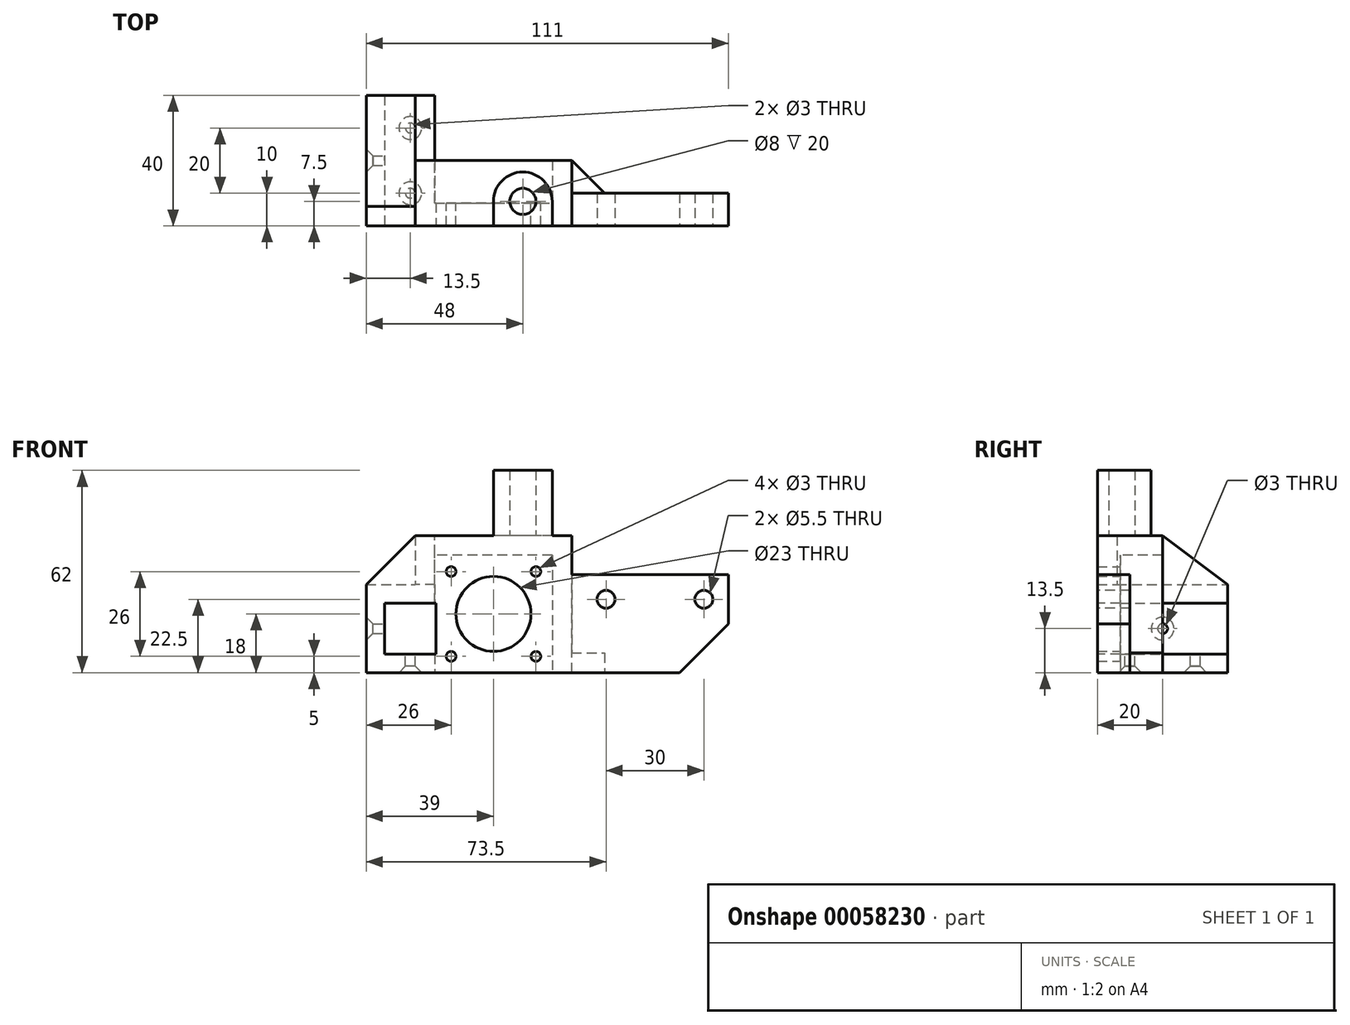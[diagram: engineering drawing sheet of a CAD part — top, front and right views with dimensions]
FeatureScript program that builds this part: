
annotation { "Feature Type Name" : "Feature", "Feature Type Description" : "" }
export const myFeature = defineFeature(function(context is Context, id is Id, definition is map)
    precondition{}
    {
        {
            var Q0;
            Q0=qCreatedBy(makeId("Front.planeOp"),FACE);
            var sketch = newSketch(context, id + "F0", { "sketchPlane" : qUnion([Q0])});
            skLineSegment(sketch, "E0.bottom", {"start": v(13, 13) * mm, "end": v(-13, 13) * mm, "construction": true});
            skLineSegment(sketch, "E0.top", {"start": v(13, -13) * mm, "end": v(-13, -13) * mm, "construction": true});
            skLineSegment(sketch, "E0.left", {"start": v(13, 13) * mm, "end": v(13, -13) * mm, "construction": true});
            skLineSegment(sketch, "E0.right", {"start": v(-13, 13) * mm, "end": v(-13, -13) * mm, "construction": true});
            skPoint(sketch, "E0.middle", {"position": v(0, 0) * mm});
            skLineSegment(sketch, "E1.bottom", {"start": v(18, 18) * mm, "end": v(-18, 18) * mm});
            skLineSegment(sketch, "E1.top", {"start": v(18, -18) * mm, "end": v(-18, -18) * mm});
            skLineSegment(sketch, "E1.left", {"start": v(18, 18) * mm, "end": v(18, -18) * mm});
            skLineSegment(sketch, "E1.right", {"start": v(-18, 18) * mm, "end": v(-18, -18) * mm, "construction": true});
            skCircle(sketch, "E2", {"center": v(-13, 13) * mm, "radius": 1.5 * mm});
            skCircle(sketch, "E3", {"center": v(13, 13) * mm, "radius": 1.5 * mm});
            skCircle(sketch, "E4", {"center": v(-13, -13) * mm, "radius": 1.5 * mm});
            skCircle(sketch, "E5", {"center": v(13, -13) * mm, "radius": 1.5 * mm});
            skLineSegment(sketch, "E6", {"start": v(-18, -18) * mm, "end": v(-33, -18) * mm});
            skLineSegment(sketch, "E7", {"start": v(-33, -18) * mm, "end": v(-33, -12) * mm, "construction": true});
            skLineSegment(sketch, "E8", {"start": v(-33, -12) * mm, "end": v(-18, -12) * mm});
            skLineSegment(sketch, "E9", {"start": v(-18, -12) * mm, "end": v(-18, 3) * mm});
            skLineSegment(sketch, "E10", {"start": v(-18, 3) * mm, "end": v(-33, 3) * mm});
            skLineSegment(sketch, "E11", {"start": v(-33, 3) * mm, "end": v(-33, 9) * mm, "construction": true});
            skLineSegment(sketch, "E12", {"start": v(-33, 9) * mm, "end": v(-18, 9) * mm});
            skLineSegment(sketch, "E13", {"start": v(-18, 9) * mm, "end": v(-18, 18) * mm});
            skPoint(sketch, "E14", {"position": v(-18, 0) * mm});
            skCircle(sketch, "E15", {"center": v(0, 0) * mm, "radius": 11.5 * mm});
            skLineSegment(sketch, "E16", {"start": v(-33, 3) * mm, "end": v(-33, -12) * mm});
            skLineSegment(sketch, "E17", {"start": v(-33, 9) * mm, "end": v(-39, 9) * mm});
            skLineSegment(sketch, "E18", {"start": v(-39, 9) * mm, "end": v(-39, -18) * mm});
            skLineSegment(sketch, "E19", {"start": v(-39, -18) * mm, "end": v(-33, -18) * mm});
            skSolve(sketch);
        }
        {
            var Q0;
            Q0 = qSketchRegion(id + "F0", true);
            extrude(context, id + "F1", {"entities" : qUnion([Q0]), "depth" : 5 * mm});
        }
        {
            var Q0;
            Q0=makeQuery(id+"F1.opExtrude","CAP_FACE",FACE,{"disambiguationData":[OSD([sQuery(id+"F0.wireOp",EDGE,"E1.bottom"),sQuery(id+"F0.wireOp",EDGE,"E1.top"),sQuery(id+"F0.wireOp",EDGE,"E1.left"),sQuery(id+"F0.wireOp",EDGE,"E2"),sQuery(id+"F0.wireOp",EDGE,"E3"),sQuery(id+"F0.wireOp",EDGE,"E4"),sQuery(id+"F0.wireOp",EDGE,"E5"),sQuery(id+"F0.wireOp",EDGE,"E6"),sQuery(id+"F0.wireOp",EDGE,"E8"),sQuery(id+"F0.wireOp",EDGE,"E9"),sQuery(id+"F0.wireOp",EDGE,"E10"),sQuery(id+"F0.wireOp",EDGE,"E12"),sQuery(id+"F0.wireOp",EDGE,"E13"),sQuery(id+"F0.wireOp",EDGE,"E15"),sQuery(id+"F0.wireOp",EDGE,"E16"),sQuery(id+"F0.wireOp",EDGE,"E17"),sQuery(id+"F0.wireOp",EDGE,"E18"),sQuery(id+"F0.wireOp",EDGE,"E19")])],"isStart":true});
            var sketch = newSketch(context, id + "F2", { "sketchPlane" : qUnion([Q0])});
            skLineSegment(sketch, "E20.0", {"start": v(18, 3) * mm, "end": v(33, 3) * mm});
            skLineSegment(sketch, "E20.1", {"start": v(33, 3) * mm, "end": v(33, -12) * mm});
            skLineSegment(sketch, "E20.2", {"start": v(33, -12) * mm, "end": v(18, -12) * mm});
            skLineSegment(sketch, "E20.3", {"start": v(39, 9) * mm, "end": v(39, -18) * mm});
            skLineSegment(sketch, "E20.4", {"start": v(39, 9) * mm, "end": v(18, 9) * mm});
            skLineSegment(sketch, "E21", {"start": v(18, 9) * mm, "end": v(18, 3) * mm});
            skLineSegment(sketch, "E22", {"start": v(18, -12) * mm, "end": v(18, -18) * mm});
            skLineSegment(sketch, "E23", {"start": v(18, -18) * mm, "end": v(39, -18) * mm});
            skSolve(sketch);
        }
        {
            var Q0;
            Q0 = qSketchRegion(id + "F2", true);
            extrude(context, id + "F3", {"entities" : qUnion([Q0]), "operationType" : NewBodyOperationType.ADD, "depth" : 35 * mm});
        }
        {
            var Q0;
            Q0=makeQuery(id+"F1.opExtrude","CAP_FACE",FACE,{"disambiguationData":[OSD([sQuery(id+"F0.wireOp",EDGE,"E1.bottom"),sQuery(id+"F0.wireOp",EDGE,"E1.top"),sQuery(id+"F0.wireOp",EDGE,"E1.left"),sQuery(id+"F0.wireOp",EDGE,"E2"),sQuery(id+"F0.wireOp",EDGE,"E3"),sQuery(id+"F0.wireOp",EDGE,"E4"),sQuery(id+"F0.wireOp",EDGE,"E5"),sQuery(id+"F0.wireOp",EDGE,"E6"),sQuery(id+"F0.wireOp",EDGE,"E8"),sQuery(id+"F0.wireOp",EDGE,"E9"),sQuery(id+"F0.wireOp",EDGE,"E10"),sQuery(id+"F0.wireOp",EDGE,"E12"),sQuery(id+"F0.wireOp",EDGE,"E13"),sQuery(id+"F0.wireOp",EDGE,"E15"),sQuery(id+"F0.wireOp",EDGE,"E16"),sQuery(id+"F0.wireOp",EDGE,"E17"),sQuery(id+"F0.wireOp",EDGE,"E18"),sQuery(id+"F0.wireOp",EDGE,"E19")])],"isStart":false});
            var sketch = newSketch(context, id + "F4", { "sketchPlane" : qUnion([Q0])});
            skLineSegment(sketch, "E24.0", {"start": v(-18, 9) * mm, "end": v(-18, 18) * mm});
            skLineSegment(sketch, "E24.1", {"start": v(18, 18) * mm, "end": v(-18, 18) * mm});
            skLineSegment(sketch, "E25", {"start": v(18, 18) * mm, "end": v(18, 24) * mm});
            skLineSegment(sketch, "E26", {"start": v(18, 24) * mm, "end": v(-24, 24) * mm});
            skLineSegment(sketch, "E27", {"start": v(-24, 24) * mm, "end": v(-24, 9) * mm});
            skLineSegment(sketch, "E28", {"start": v(-24, 9) * mm, "end": v(-18, 9) * mm});
            skSolve(sketch);
        }
        {
            var Q0;
            Q0 = qSketchRegion(id + "F4", true);
            var Q1;
            Q1=makeQuery(id+"F3.opExtrude","CAP_FACE",FACE,{"disambiguationData":[OSD([sQuery(id+"F2.wireOp",EDGE,"E20.0"),sQuery(id+"F2.wireOp",EDGE,"E20.1"),sQuery(id+"F2.wireOp",EDGE,"E20.2"),sQuery(id+"F2.wireOp",EDGE,"E20.3"),sQuery(id+"F2.wireOp",EDGE,"E20.4"),sQuery(id+"F2.wireOp",EDGE,"E21"),sQuery(id+"F2.wireOp",EDGE,"E22"),sQuery(id+"F2.wireOp",EDGE,"E23")])],"isStart":false});
            extrude(context, id + "F5", {"entities" : qUnion([Q0]), "operationType" : NewBodyOperationType.ADD, "oppositeDirection" : true, "endBoundEntityFace" : qUnion([Q1]), "depth" : 20 * mm});
        }
        {
            var Q0;
            Q0=makeQuery(id+"F3.boolean.opBoolean","MERGE",FACE,{"derivedFrom":[makeQuery(id+"F1.opExtrude","SWEPT_FACE",FACE,{"disambiguationData":[OSD([sQuery(id+"F0.wireOp",EDGE,"E16")])]}),makeQuery(id+"F3.opExtrude","SWEPT_FACE",FACE,{"disambiguationData":[OSD([sQuery(id+"F2.wireOp",EDGE,"E20.1")])]})]});
            var sketch = newSketch(context, id + "F6", { "sketchPlane" : qUnion([Q0])});
            skLineSegment(sketch, "E29", {"start": v(35, -4.5) * mm, "end": v(-5, -4.5) * mm, "construction": true});
            skCircle(sketch, "E30", {"center": v(15, -4.5) * mm, "radius": 1.5 * mm});
            skSolve(sketch);
        }
        {
            var Q0;
            Q0 = qSketchRegion(id + "F6", true);
            extrude(context, id + "F7", {"entities" : qUnion([Q0]), "operationType" : NewBodyOperationType.REMOVE, "endBound" : BoundingType.THROUGH_ALL, "oppositeDirection" : true, "depth" : 25 * mm});
        }
        {
            var Q0;
            Q0=makeQuery(id+"F5.opExtrude","SWEPT_FACE",FACE,{"disambiguationData":[OSD([sQuery(id+"F4.wireOp",EDGE,"E27")])]});
            var sketch = newSketch(context, id + "F8", { "sketchPlane" : qUnion([Q0])});
            skLineSegment(sketch, "E31", {"start": v(-15, 24) * mm, "end": v(-35, 9) * mm});
            skLineSegment(sketch, "E32.0", {"start": v(-15, 24) * mm, "end": v(-15, 9) * mm});
            skLineSegment(sketch, "E33", {"start": v(-15, 9) * mm, "end": v(-35, 9) * mm});
            skSolve(sketch);
        }
        {
            var Q0;
            Q0 = qSketchRegion(id + "F8", true);
            var Q1;
            Q1=makeQuery(id+"F5.boolean.opBoolean","MERGE",FACE,{"derivedFrom":[makeQuery(id+"F3.opExtrude","SWEPT_FACE",FACE,{"disambiguationData":[OSD([sQuery(id+"F2.wireOp",EDGE,"E21")])]}),makeQuery(id+"F5.opExtrude","SWEPT_FACE",FACE,{"disambiguationData":[OSD([sQuery(id+"F4.wireOp",EDGE,"E24.0")])]})]});
            extrude(context, id + "F9", {"entities" : qUnion([Q0]), "operationType" : NewBodyOperationType.ADD, "endBound" : BoundingType.UP_TO_SURFACE, "oppositeDirection" : true, "endBoundEntityFace" : qUnion([Q1]), "depth" : 25 * mm});
        }
        {
            var Q0;
            Q0=makeQuery(id+"F5.boolean.opBoolean","MERGE",FACE,{"derivedFrom":[makeQuery(id+"F1.opExtrude","CAP_FACE",FACE,{"disambiguationData":[OSD([sQuery(id+"F0.wireOp",EDGE,"E1.bottom"),sQuery(id+"F0.wireOp",EDGE,"E1.top"),sQuery(id+"F0.wireOp",EDGE,"E1.left"),sQuery(id+"F0.wireOp",EDGE,"E2"),sQuery(id+"F0.wireOp",EDGE,"E3"),sQuery(id+"F0.wireOp",EDGE,"E4"),sQuery(id+"F0.wireOp",EDGE,"E5"),sQuery(id+"F0.wireOp",EDGE,"E6"),sQuery(id+"F0.wireOp",EDGE,"E8"),sQuery(id+"F0.wireOp",EDGE,"E9"),sQuery(id+"F0.wireOp",EDGE,"E10"),sQuery(id+"F0.wireOp",EDGE,"E12"),sQuery(id+"F0.wireOp",EDGE,"E13"),sQuery(id+"F0.wireOp",EDGE,"E15"),sQuery(id+"F0.wireOp",EDGE,"E16"),sQuery(id+"F0.wireOp",EDGE,"E17"),sQuery(id+"F0.wireOp",EDGE,"E18"),sQuery(id+"F0.wireOp",EDGE,"E19")])],"isStart":false}),makeQuery(id+"F5.opExtrude","CAP_FACE",FACE,{"disambiguationData":[OSD([sQuery(id+"F4.wireOp",EDGE,"E24.0"),sQuery(id+"F4.wireOp",EDGE,"E24.1"),sQuery(id+"F4.wireOp",EDGE,"E25"),sQuery(id+"F4.wireOp",EDGE,"E26"),sQuery(id+"F4.wireOp",EDGE,"E27"),sQuery(id+"F4.wireOp",EDGE,"E28")])],"isStart":true})]});
            var sketch = newSketch(context, id + "F10", { "sketchPlane" : qUnion([Q0])});
            skLineSegment(sketch, "E34", {"start": v(-24, 24) * mm, "end": v(-39, 9) * mm});
            skLineSegment(sketch, "E35.0", {"start": v(-39, 9) * mm, "end": v(-24, 9) * mm});
            skLineSegment(sketch, "E35.1", {"start": v(-24, 24) * mm, "end": v(-24, 9) * mm});
            skSolve(sketch);
        }
        {
            var Q0;
            Q0 = qSketchRegion(id + "F10", true);
            var Q1;
            Q1=makeQuery(id+"F1.opExtrude","CAP_FACE",FACE,{"disambiguationData":[OSD([sQuery(id+"F0.wireOp",EDGE,"E1.bottom"),sQuery(id+"F0.wireOp",EDGE,"E1.top"),sQuery(id+"F0.wireOp",EDGE,"E1.left"),sQuery(id+"F0.wireOp",EDGE,"E2"),sQuery(id+"F0.wireOp",EDGE,"E3"),sQuery(id+"F0.wireOp",EDGE,"E4"),sQuery(id+"F0.wireOp",EDGE,"E5"),sQuery(id+"F0.wireOp",EDGE,"E6"),sQuery(id+"F0.wireOp",EDGE,"E8"),sQuery(id+"F0.wireOp",EDGE,"E9"),sQuery(id+"F0.wireOp",EDGE,"E10"),sQuery(id+"F0.wireOp",EDGE,"E12"),sQuery(id+"F0.wireOp",EDGE,"E13"),sQuery(id+"F0.wireOp",EDGE,"E15"),sQuery(id+"F0.wireOp",EDGE,"E16"),sQuery(id+"F0.wireOp",EDGE,"E17"),sQuery(id+"F0.wireOp",EDGE,"E18"),sQuery(id+"F0.wireOp",EDGE,"E19")])],"isStart":true});
            extrude(context, id + "F11", {"entities" : qUnion([Q0]), "operationType" : NewBodyOperationType.ADD, "oppositeDirection" : true, "endBoundEntityFace" : qUnion([Q1]), "depth" : 6 * mm});
        }
        {
            var Q0;
            Q0=makeQuery(id+"F3.boolean.opBoolean","MERGE",FACE,{"derivedFrom":[makeQuery(id+"F1.opExtrude","SWEPT_FACE",FACE,{"disambiguationData":[OSD([sQuery(id+"F0.wireOp",EDGE,"E8")])]}),makeQuery(id+"F3.opExtrude","SWEPT_FACE",FACE,{"disambiguationData":[OSD([sQuery(id+"F2.wireOp",EDGE,"E20.2")])]})]});
            var sketch = newSketch(context, id + "F12", { "sketchPlane" : qUnion([Q0])});
            skLineSegment(sketch, "E36", {"start": v(-25.5, -5) * mm, "end": v(-25.5, 35) * mm, "construction": true});
            skCircle(sketch, "E37", {"center": v(-25.5, 5) * mm, "radius": 1.5 * mm});
            skCircle(sketch, "E38", {"center": v(-25.5, 25) * mm, "radius": 1.5 * mm});
            skSolve(sketch);
        }
        {
            var Q0;
            Q0 = qSketchRegion(id + "F12", true);
            extrude(context, id + "F13", {"entities" : qUnion([Q0]), "operationType" : NewBodyOperationType.REMOVE, "endBound" : BoundingType.THROUGH_ALL, "oppositeDirection" : true, "depth" : 25 * mm});
        }
        {
            var Q0;
            Q0=makeQuery(id+"F5.boolean.opBoolean","MERGE",FACE,{"derivedFrom":[makeQuery(id+"F1.opExtrude","SWEPT_FACE",FACE,{"disambiguationData":[OSD([sQuery(id+"F0.wireOp",EDGE,"E1.left")])]}),makeQuery(id+"F5.opExtrude","SWEPT_FACE",FACE,{"disambiguationData":[OSD([sQuery(id+"F4.wireOp",EDGE,"E25")])]})]});
            var sketch = newSketch(context, id + "F14", { "sketchPlane" : qUnion([Q0])});
            skLineSegment(sketch, "E39.bottom", {"start": v(-5, 24) * mm, "end": v(15, 24) * mm});
            skLineSegment(sketch, "E39.top", {"start": v(-5, -18) * mm, "end": v(15, -18) * mm});
            skLineSegment(sketch, "E39.left", {"start": v(-5, 24) * mm, "end": v(-5, -18) * mm});
            skLineSegment(sketch, "E39.right", {"start": v(15, 24) * mm, "end": v(15, -18) * mm});
            skSolve(sketch);
        }
        {
            var Q0;
            Q0 = qSketchRegion(id + "F14", true);
            extrude(context, id + "F15", {"entities" : qUnion([Q0]), "operationType" : NewBodyOperationType.ADD, "depth" : 6 * mm});
        }
        {
            var Q0;
            Q0=makeQuery(id+"F15.boolean.opBoolean","MERGE",FACE,{"derivedFrom":[makeQuery(id+"F11.boolean.opBoolean","MERGE",FACE,{"derivedFrom":[makeQuery(id+"F5.boolean.opBoolean","MERGE",FACE,{"derivedFrom":[makeQuery(id+"F1.opExtrude","CAP_FACE",FACE,{"disambiguationData":[OSD([sQuery(id+"F0.wireOp",EDGE,"E1.bottom"),sQuery(id+"F0.wireOp",EDGE,"E1.top"),sQuery(id+"F0.wireOp",EDGE,"E1.left"),sQuery(id+"F0.wireOp",EDGE,"E2"),sQuery(id+"F0.wireOp",EDGE,"E3"),sQuery(id+"F0.wireOp",EDGE,"E4"),sQuery(id+"F0.wireOp",EDGE,"E5"),sQuery(id+"F0.wireOp",EDGE,"E6"),sQuery(id+"F0.wireOp",EDGE,"E8"),sQuery(id+"F0.wireOp",EDGE,"E9"),sQuery(id+"F0.wireOp",EDGE,"E10"),sQuery(id+"F0.wireOp",EDGE,"E12"),sQuery(id+"F0.wireOp",EDGE,"E13"),sQuery(id+"F0.wireOp",EDGE,"E15"),sQuery(id+"F0.wireOp",EDGE,"E16"),sQuery(id+"F0.wireOp",EDGE,"E17"),sQuery(id+"F0.wireOp",EDGE,"E18"),sQuery(id+"F0.wireOp",EDGE,"E19")])],"isStart":false}),makeQuery(id+"F5.opExtrude","CAP_FACE",FACE,{"disambiguationData":[OSD([sQuery(id+"F4.wireOp",EDGE,"E24.0"),sQuery(id+"F4.wireOp",EDGE,"E24.1"),sQuery(id+"F4.wireOp",EDGE,"E25"),sQuery(id+"F4.wireOp",EDGE,"E26"),sQuery(id+"F4.wireOp",EDGE,"E27"),sQuery(id+"F4.wireOp",EDGE,"E28")])],"isStart":true})]}),makeQuery(id+"F11.opExtrude","CAP_FACE",FACE,{"disambiguationData":[OSD([sQuery(id+"F10.wireOp",EDGE,"E34"),sQuery(id+"F10.wireOp",EDGE,"E35.0"),sQuery(id+"F10.wireOp",EDGE,"E35.1")])],"isStart":true})]}),makeQuery(id+"F15.opExtrude","SWEPT_FACE",FACE,{"disambiguationData":[OSD([sQuery(id+"F14.wireOp",EDGE,"E39.left")])]})]});
            var sketch = newSketch(context, id + "F16", { "sketchPlane" : qUnion([Q0])});
            skCircle(sketch, "E40", {"center": v(0, 0) * mm, "radius": 9 * mm, "construction": true});
            skCircle(sketch, "E41", {"center": v(34.5, 4.5) * mm, "radius": 7.5 * mm, "construction": true});
            skCircle(sketch, "E42", {"center": v(49.5, 4.5) * mm, "radius": 7.5 * mm, "construction": true});
            skCircle(sketch, "E43", {"center": v(64.5, 4.5) * mm, "radius": 7.5 * mm, "construction": true});
            skPoint(sketch, "E44", {"position": v(34.5, -3) * mm});
            skCircle(sketch, "E45", {"center": v(34.5, 4.5) * mm, "radius": 2.75 * mm});
            skCircle(sketch, "E46", {"center": v(64.5, 4.5) * mm, "radius": 2.75 * mm});
            skLineSegment(sketch, "E47", {"start": v(-9, 0) * mm, "end": v(-1.5, 0) * mm, "construction": true});
            skLineSegment(sketch, "E48", {"start": v(24, -18) * mm, "end": v(57, -18) * mm});
            skLineSegment(sketch, "E49", {"start": v(57, -18) * mm, "end": v(72, -3) * mm});
            skLineSegment(sketch, "E50", {"start": v(72, -3) * mm, "end": v(72, 12) * mm});
            skLineSegment(sketch, "E51", {"start": v(72, 12) * mm, "end": v(24, 12) * mm});
            skLineSegment(sketch, "E52", {"start": v(24, 12) * mm, "end": v(24, -18) * mm});
            skSolve(sketch);
        }
        {
            var Q0;
            Q0 = qSketchRegion(id + "F16", true);
            var Q1;
            Q1=makeQuery(id+"F15.boolean.opBoolean","MERGE",FACE,{"derivedFrom":[makeQuery(id+"F5.opExtrude","CAP_FACE",FACE,{"disambiguationData":[OSD([sQuery(id+"F4.wireOp",EDGE,"E24.0"),sQuery(id+"F4.wireOp",EDGE,"E24.1"),sQuery(id+"F4.wireOp",EDGE,"E25"),sQuery(id+"F4.wireOp",EDGE,"E26"),sQuery(id+"F4.wireOp",EDGE,"E27"),sQuery(id+"F4.wireOp",EDGE,"E28")])],"isStart":false}),makeQuery(id+"F15.opExtrude","SWEPT_FACE",FACE,{"disambiguationData":[OSD([sQuery(id+"F14.wireOp",EDGE,"E39.right")])]})]});
            extrude(context, id + "F17", {"entities" : qUnion([Q0]), "operationType" : NewBodyOperationType.ADD, "oppositeDirection" : true, "endBoundEntityFace" : qUnion([Q1]), "depth" : 10 * mm});
        }
        {
            var Q0;
            Q0=makeQuery(id+"F17.boolean.opBoolean","MERGE",FACE,{"derivedFrom":[makeQuery(id+"F15.boolean.opBoolean","MERGE",FACE,{"derivedFrom":[makeQuery(id+"F3.boolean.opBoolean","MERGE",FACE,{"derivedFrom":[makeQuery(id+"F1.opExtrude","SWEPT_FACE",FACE,{"disambiguationData":[OSD([sQuery(id+"F0.wireOp",EDGE,"E1.top"),sQuery(id+"F0.wireOp",EDGE,"E6"),sQuery(id+"F0.wireOp",EDGE,"E19")])]}),makeQuery(id+"F3.opExtrude","SWEPT_FACE",FACE,{"disambiguationData":[OSD([sQuery(id+"F2.wireOp",EDGE,"E23")])]})]}),makeQuery(id+"F15.opExtrude","SWEPT_FACE",FACE,{"disambiguationData":[OSD([sQuery(id+"F14.wireOp",EDGE,"E39.top")])]})]}),makeQuery(id+"F17.opExtrude","SWEPT_FACE",FACE,{"disambiguationData":[OSD([sQuery(id+"F16.wireOp",EDGE,"E48")])]})]});
            var sketch = newSketch(context, id + "F18", { "sketchPlane" : qUnion([Q0])});
            skLineSegment(sketch, "E53.0", {"start": v(24, -5) * mm, "end": v(24, -15) * mm});
            skLineSegment(sketch, "E54", {"start": v(24, -15) * mm, "end": v(34, -5) * mm});
            skLineSegment(sketch, "E55", {"start": v(34, -5) * mm, "end": v(24, -5) * mm});
            skSolve(sketch);
        }
        {
            var Q0;
            Q0 = qSketchRegion(id + "F18", true);
            var Q1;
            Q1=makeQuery(id+"F3.boolean.opBoolean","MERGE",FACE,{"derivedFrom":[makeQuery(id+"F1.opExtrude","SWEPT_FACE",FACE,{"disambiguationData":[OSD([sQuery(id+"F0.wireOp",EDGE,"E8")])]}),makeQuery(id+"F3.opExtrude","SWEPT_FACE",FACE,{"disambiguationData":[OSD([sQuery(id+"F2.wireOp",EDGE,"E20.2")])]})]});
            extrude(context, id + "F19", {"entities" : qUnion([Q0]), "operationType" : NewBodyOperationType.ADD, "endBound" : BoundingType.UP_TO_SURFACE, "oppositeDirection" : true, "endBoundEntityFace" : qUnion([Q1]), "depth" : 25 * mm});
        }
        {
            var Q0;
            Q0=makeQuery(id+"F7.boolean.opBoolean","INTERSECT",EDGE,{"derivedFrom":[makeQuery(id+"F3.boolean.opBoolean","MERGE",FACE,{"derivedFrom":[makeQuery(id+"F1.opExtrude","SWEPT_FACE",FACE,{"disambiguationData":[OSD([sQuery(id+"F0.wireOp",EDGE,"E18")])]}),makeQuery(id+"F3.opExtrude","SWEPT_FACE",FACE,{"disambiguationData":[OSD([sQuery(id+"F2.wireOp",EDGE,"E20.3")])]})]}),makeQuery(id+"F7.opExtrude","SWEPT_FACE",FACE,{"disambiguationData":[OSD([sQuery(id+"F6.wireOp",EDGE,"E30")])]})]});
            var Q1;
            Q1=makeQuery(id+"F13.boolean.opBoolean","INTERSECT",EDGE,{"derivedFrom":[makeQuery(id+"F3.boolean.opBoolean","MERGE",FACE,{"derivedFrom":[makeQuery(id+"F1.opExtrude","SWEPT_FACE",FACE,{"disambiguationData":[OSD([sQuery(id+"F0.wireOp",EDGE,"E1.top"),sQuery(id+"F0.wireOp",EDGE,"E6"),sQuery(id+"F0.wireOp",EDGE,"E19")])]}),makeQuery(id+"F3.opExtrude","SWEPT_FACE",FACE,{"disambiguationData":[OSD([sQuery(id+"F2.wireOp",EDGE,"E23")])]})]}),makeQuery(id+"F13.opExtrude","SWEPT_FACE",FACE,{"disambiguationData":[OSD([sQuery(id+"F12.wireOp",EDGE,"E37")])]})]});
            var Q2;
            Q2=makeQuery(id+"F13.boolean.opBoolean","INTERSECT",EDGE,{"derivedFrom":[makeQuery(id+"F3.boolean.opBoolean","MERGE",FACE,{"derivedFrom":[makeQuery(id+"F1.opExtrude","SWEPT_FACE",FACE,{"disambiguationData":[OSD([sQuery(id+"F0.wireOp",EDGE,"E1.top"),sQuery(id+"F0.wireOp",EDGE,"E6"),sQuery(id+"F0.wireOp",EDGE,"E19")])]}),makeQuery(id+"F3.opExtrude","SWEPT_FACE",FACE,{"disambiguationData":[OSD([sQuery(id+"F2.wireOp",EDGE,"E23")])]})]}),makeQuery(id+"F13.opExtrude","SWEPT_FACE",FACE,{"disambiguationData":[OSD([sQuery(id+"F12.wireOp",EDGE,"E38")])]})]});
            chamfer(context, id + "F20", {"entities" : qUnion([Q0, Q1, Q2]), "width" : 2 * mm, "tangentPropagation" : true});
        }
        {
            var Q0;
            Q0=makeQuery(id+"F17.boolean.opBoolean","MERGE",FACE,{"derivedFrom":[makeQuery(id+"F15.boolean.opBoolean","MERGE",FACE,{"derivedFrom":[makeQuery(id+"F11.boolean.opBoolean","MERGE",FACE,{"derivedFrom":[makeQuery(id+"F5.boolean.opBoolean","MERGE",FACE,{"derivedFrom":[makeQuery(id+"F1.opExtrude","CAP_FACE",FACE,{"disambiguationData":[OSD([sQuery(id+"F0.wireOp",EDGE,"E1.bottom"),sQuery(id+"F0.wireOp",EDGE,"E1.top"),sQuery(id+"F0.wireOp",EDGE,"E1.left"),sQuery(id+"F0.wireOp",EDGE,"E2"),sQuery(id+"F0.wireOp",EDGE,"E3"),sQuery(id+"F0.wireOp",EDGE,"E4"),sQuery(id+"F0.wireOp",EDGE,"E5"),sQuery(id+"F0.wireOp",EDGE,"E6"),sQuery(id+"F0.wireOp",EDGE,"E8"),sQuery(id+"F0.wireOp",EDGE,"E9"),sQuery(id+"F0.wireOp",EDGE,"E10"),sQuery(id+"F0.wireOp",EDGE,"E12"),sQuery(id+"F0.wireOp",EDGE,"E13"),sQuery(id+"F0.wireOp",EDGE,"E15"),sQuery(id+"F0.wireOp",EDGE,"E16"),sQuery(id+"F0.wireOp",EDGE,"E17"),sQuery(id+"F0.wireOp",EDGE,"E18"),sQuery(id+"F0.wireOp",EDGE,"E19")])],"isStart":false}),makeQuery(id+"F5.opExtrude","CAP_FACE",FACE,{"disambiguationData":[OSD([sQuery(id+"F4.wireOp",EDGE,"E24.0"),sQuery(id+"F4.wireOp",EDGE,"E24.1"),sQuery(id+"F4.wireOp",EDGE,"E25"),sQuery(id+"F4.wireOp",EDGE,"E26"),sQuery(id+"F4.wireOp",EDGE,"E27"),sQuery(id+"F4.wireOp",EDGE,"E28")])],"isStart":true})]}),makeQuery(id+"F11.opExtrude","CAP_FACE",FACE,{"disambiguationData":[OSD([sQuery(id+"F10.wireOp",EDGE,"E34"),sQuery(id+"F10.wireOp",EDGE,"E35.0"),sQuery(id+"F10.wireOp",EDGE,"E35.1")])],"isStart":true})]}),makeQuery(id+"F15.opExtrude","SWEPT_FACE",FACE,{"disambiguationData":[OSD([sQuery(id+"F14.wireOp",EDGE,"E39.left")])]})]}),makeQuery(id+"F17.opExtrude","CAP_FACE",FACE,{"disambiguationData":[OSD([sQuery(id+"F16.wireOp",EDGE,"E45"),sQuery(id+"F16.wireOp",EDGE,"E46"),sQuery(id+"F16.wireOp",EDGE,"E48"),sQuery(id+"F16.wireOp",EDGE,"E49"),sQuery(id+"F16.wireOp",EDGE,"E50"),sQuery(id+"F16.wireOp",EDGE,"E51"),sQuery(id+"F16.wireOp",EDGE,"E52")])],"isStart":true})]});
            var sketch = newSketch(context, id + "F21", { "sketchPlane" : qUnion([Q0])});
            skLineSegment(sketch, "E56", {"start": v(-33, 3) * mm, "end": v(-18, -12) * mm, "construction": true});
            skLineSegment(sketch, "E57.bottom", {"start": v(-17.65, 3.35) * mm, "end": v(-33.35, 3.35) * mm});
            skLineSegment(sketch, "E57.top", {"start": v(-17.65, -12.35) * mm, "end": v(-33.35, -12.35) * mm});
            skLineSegment(sketch, "E57.left", {"start": v(-17.65, 3.35) * mm, "end": v(-17.65, -12.35) * mm});
            skLineSegment(sketch, "E57.right", {"start": v(-33.35, 3.35) * mm, "end": v(-33.35, -12.35) * mm});
            skPoint(sketch, "E57.middle", {"position": v(-25.5, -4.5) * mm});
            skSolve(sketch);
        }
        {
            var Q0;
            Q0 = qSketchRegion(id + "F21", true);
            extrude(context, id + "F22", {"entities" : qUnion([Q0]), "operationType" : NewBodyOperationType.REMOVE, "endBound" : BoundingType.THROUGH_ALL, "oppositeDirection" : true, "depth" : 25 * mm});
        }
        {
            var Q0;
            Q0=makeQuery(id+"F1.opExtrude","CAP_FACE",FACE,{"disambiguationData":[OSD([sQuery(id+"F0.wireOp",EDGE,"E1.bottom"),sQuery(id+"F0.wireOp",EDGE,"E1.top"),sQuery(id+"F0.wireOp",EDGE,"E1.left"),sQuery(id+"F0.wireOp",EDGE,"E2"),sQuery(id+"F0.wireOp",EDGE,"E3"),sQuery(id+"F0.wireOp",EDGE,"E4"),sQuery(id+"F0.wireOp",EDGE,"E5"),sQuery(id+"F0.wireOp",EDGE,"E6"),sQuery(id+"F0.wireOp",EDGE,"E8"),sQuery(id+"F0.wireOp",EDGE,"E9"),sQuery(id+"F0.wireOp",EDGE,"E10"),sQuery(id+"F0.wireOp",EDGE,"E12"),sQuery(id+"F0.wireOp",EDGE,"E13"),sQuery(id+"F0.wireOp",EDGE,"E15"),sQuery(id+"F0.wireOp",EDGE,"E16"),sQuery(id+"F0.wireOp",EDGE,"E17"),sQuery(id+"F0.wireOp",EDGE,"E18"),sQuery(id+"F0.wireOp",EDGE,"E19")])],"isStart":true});
            extrude(context, id + "F23", {"entities" : qUnion([Q0]), "operationType" : NewBodyOperationType.ADD, "depth" : 2 * mm});
        }
        {
            var Q0;
            Q0=makeQuery(id+"F15.boolean.opBoolean","MERGE",FACE,{"derivedFrom":[makeQuery(id+"F5.opExtrude","SWEPT_FACE",FACE,{"disambiguationData":[OSD([sQuery(id+"F4.wireOp",EDGE,"E26")])]}),makeQuery(id+"F15.opExtrude","SWEPT_FACE",FACE,{"disambiguationData":[OSD([sQuery(id+"F14.wireOp",EDGE,"E39.bottom")])]})]});
            var sketch = newSketch(context, id + "F24", { "sketchPlane" : qUnion([Q0])});
            skLineSegment(sketch, "E58", {"start": v(9, -5) * mm, "end": v(9, 2.5) * mm, "construction": true});
            skCircle(sketch, "E59", {"center": v(9, 2.5) * mm, "radius": 4 * mm});
            skLineSegment(sketch, "E60", {"start": v(0, -5) * mm, "end": v(0, 2.5) * mm});
            skLineSegment(sketch, "E61.MirrorCS", {"start": v(18, -5) * mm, "end": v(18, 2.5) * mm});
            skArc(sketch, "E62", {"start": v(0, 2.5) * mm, "mid": v(9, 11.5) * mm, "end": v(18, 2.5) * mm});
            skLineSegment(sketch, "E63", {"start": v(0, -5) * mm, "end": v(18, -5) * mm});
            skSolve(sketch);
        }
        {
            var Q0;
            Q0 = qSketchRegion(id + "F24", true);
            extrude(context, id + "F25", {"entities" : qUnion([Q0]), "operationType" : NewBodyOperationType.ADD, "depth" : 20 * mm});
        }
    });
